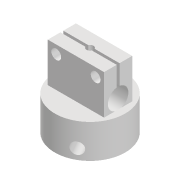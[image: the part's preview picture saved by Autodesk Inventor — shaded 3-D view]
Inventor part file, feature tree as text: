
AUTODESK INVENTOR PART (.ipt)
format: ipt  version: 2022 (Build 260153000, 153)  size: 198,144 bytes
history: native  units: in
note: dims shown in document units (in); Inventor stores cm internally (conversion verified against a paired STEP export)
features: sketch x7, extrude x5, hole x2, pattern_circular x1, projected_geometry x1
ambient origin geometry x8: Origin, YZ Plane, XZ Plane, XY Plane, X Axis, Y Axis, Z Axis, Center Point
bodies: Body1 (feature_tree)
feature tree (16):
  extrude  "Extrusion9"  Depth=0.9843in
  extrude  "Extrusion10"  Depth=0.5906in TaperAngle=0.0deg
  pattern_circular  "Circular Pattern2"  Count=3 Angle=360.0deg
  extrude  "Extrusion11"  Depth=0.3937in TaperAngle=0.0deg
  extrude  "Extrusion12"  Depth=0.0394in
  hole  "Hole1"  [1 undecoded]
  hole  "Hole2"  [1 undecoded]
  extrude  "Extrusion13"  TaperAngle=0.0deg  [1 undecoded]
  sketch  "Sketch14"  dims[d69=0.1929in d70=0.9843in]
  sketch  "Sketch15"  dims[d71=0.4724in d72=0.0in d73=0.5906in d74=0.0in d75=1.1811in d76=360.0deg]
  sketch  "Sketch16"  dims[d78=0.3937in d79=0.7874in d80=0.0in]
  sketch  "Sketch17"  dims[d81=0.5512in d82=0.0394in]
  sketch  "Sketch18"  dims[d83=0.4724in d84=0.0in d85=0.0in]
  projected_geometry  "Projected Loop3"
  sketch  "Sketch19"  dims[d86=0.1181in]
  sketch  "Sketch20"  dims[d87=0.1378in d88=0.2362in d89=0.2362in d90=0.1969in d91=90.0deg d92=0.315in d93=0.8108in d94=0.1102in d95=0.2362in d96=0.1575in d97=0.0787in d98=90.0deg d99=0.315in d100=0.8108in d101=0.0984in d102=0.0in d103=0.0in]
note: 3 required parameter values undecoded (feature->parameter linkage not recoverable at this tier; creation-order binding heuristic only, values carry confidence <= 0.55)
